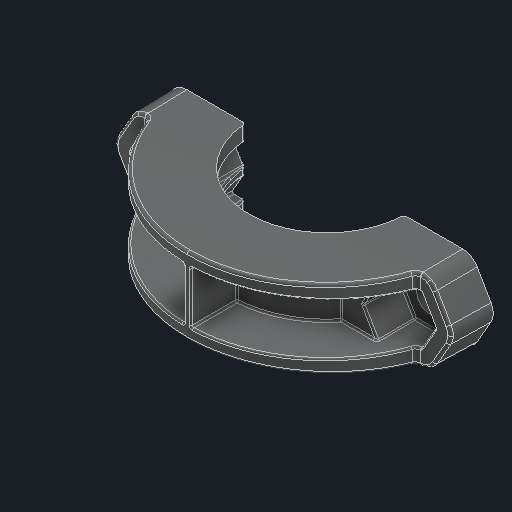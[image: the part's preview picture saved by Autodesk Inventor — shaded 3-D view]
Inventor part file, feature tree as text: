
AUTODESK INVENTOR PART (.ipt)
format: ipt  version: 2024 (Build 280153000, 153)  size: 673,792 bytes
history: native  units: in
note: dims shown in document units (in); Inventor stores cm internally (conversion verified against a paired STEP export)
features: fillet x1
ambient origin geometry x8: Origin, YZ Plane, XZ Plane, XY Plane, X Axis, Y Axis, Z Axis, Center Point
bodies: Solid1 (feature_tree)
feature tree (1):
  fillet  "Fillet22"  [1 undecoded]
note: 1 required parameter value undecoded (feature->parameter linkage not recoverable at this tier; creation-order binding heuristic only, values carry confidence <= 0.55)
